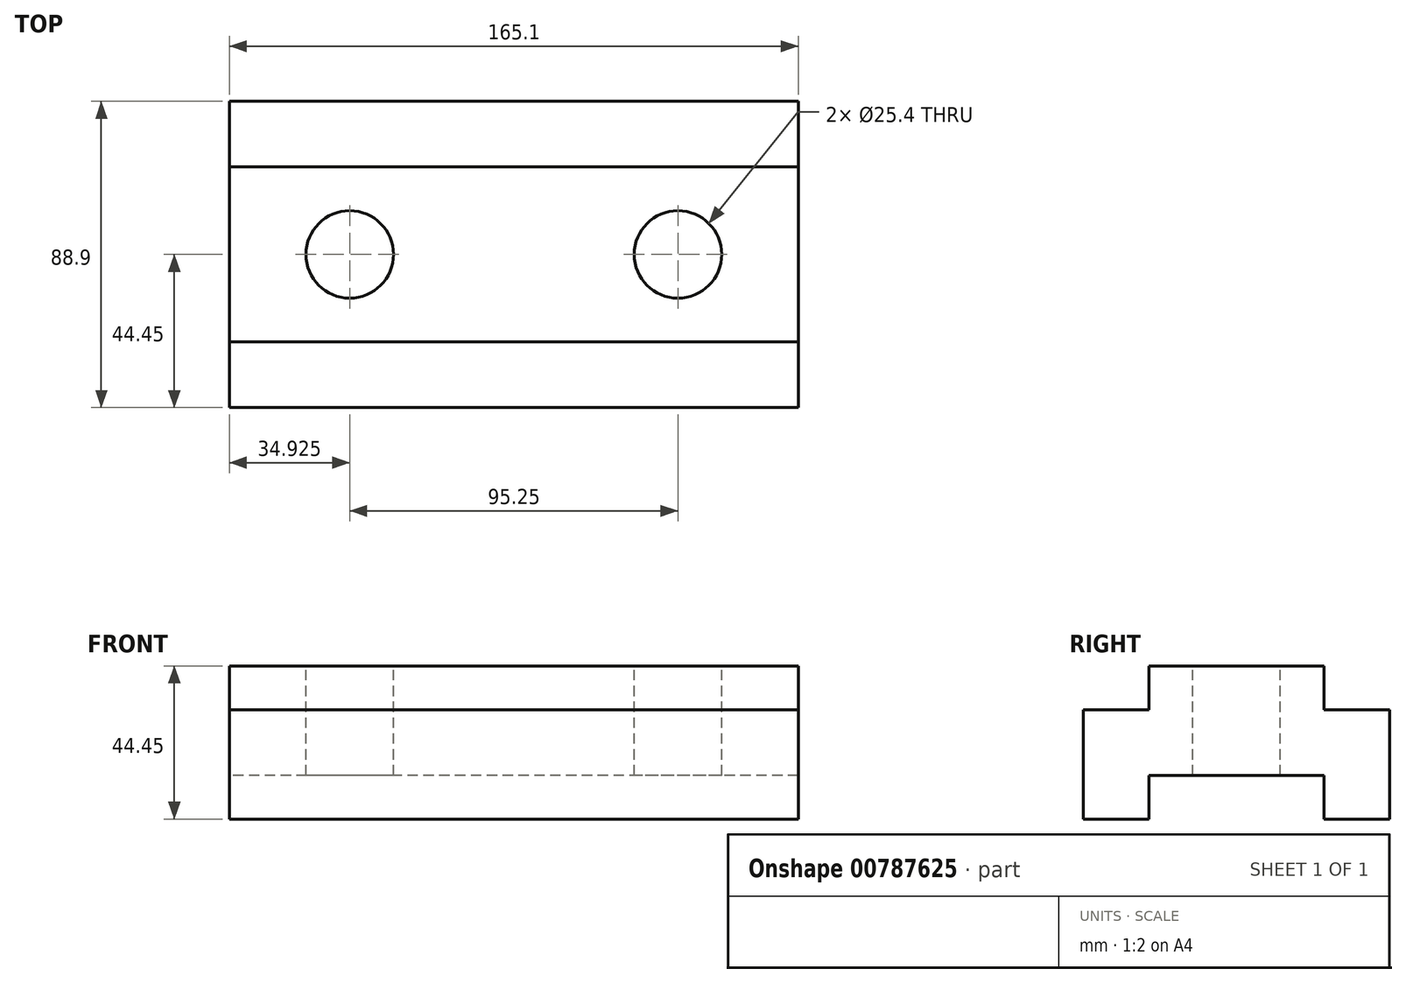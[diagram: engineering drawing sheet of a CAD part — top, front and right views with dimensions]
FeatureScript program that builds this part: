
annotation { "Feature Type Name" : "Feature", "Feature Type Description" : "" }
export const myFeature = defineFeature(function(context is Context, id is Id, definition is map)
    precondition{}
    {
        {
            var Q0;
            Q0=qCreatedBy(makeId("Right.planeOp"),FACE);
            var sketch = newSketch(context, id + "F0", { "sketchPlane" : qUnion([Q0])});
            skLineSegment(sketch, "E0", {"start": v(0, 0) * mm, "end": v(19.05, 0) * mm});
            skLineSegment(sketch, "E1", {"start": v(19.05, 0) * mm, "end": v(19.05, 12.7) * mm});
            skLineSegment(sketch, "E2", {"start": v(19.05, 12.7) * mm, "end": v(69.85, 12.7) * mm});
            skLineSegment(sketch, "E3", {"start": v(69.85, 12.7) * mm, "end": v(69.85, 0) * mm});
            skLineSegment(sketch, "E4", {"start": v(69.85, 0) * mm, "end": v(88.9, 0) * mm});
            skLineSegment(sketch, "E5", {"start": v(88.9, 0) * mm, "end": v(88.9, 31.75) * mm});
            skLineSegment(sketch, "E6", {"start": v(0, 0) * mm, "end": v(0, 31.75) * mm});
            skLineSegment(sketch, "E7", {"start": v(0, 31.75) * mm, "end": v(19.05, 31.75) * mm});
            skLineSegment(sketch, "E8", {"start": v(19.05, 31.75) * mm, "end": v(19.05, 44.45) * mm});
            skLineSegment(sketch, "E9", {"start": v(19.05, 44.45) * mm, "end": v(69.85, 44.45) * mm});
            skLineSegment(sketch, "E10", {"start": v(69.85, 44.45) * mm, "end": v(69.85, 31.75) * mm});
            skLineSegment(sketch, "E11", {"start": v(69.85, 31.75) * mm, "end": v(88.9, 31.75) * mm});
            skSolve(sketch);
        }
        {
            var Q0;
            Q0=makeQuery(id+"F0.imprint","IMPRINT",FACE,{"disambiguationData":[TD([[makeQuery(id+"F0.imprint","IMPRINT",EDGE,{"derivedFrom":sQuery(id+"F0.wireOp",EDGE,"E0")}),1.0]])]});
            extrude(context, id + "F1", {"entities" : qUnion([Q0]), "depth" : 165.1 * mm, "offsetDistance" : 25.4 * mm});
        }
        {
            var Q0;
            Q0=makeQuery(id+"F1.opExtrude","SWEPT_FACE",FACE,{"disambiguationData":[OSD([sQuery(id+"F0.wireOp",EDGE,"E9")])]});
            var sketch = newSketch(context, id + "F2", { "sketchPlane" : qUnion([Q0])});
            skLineSegment(sketch, "E12", {"start": v(0, 44.45) * mm, "end": v(34.92, 44.45) * mm, "construction": true});
            skLineSegment(sketch, "E13", {"start": v(34.92, 44.45) * mm, "end": v(130.18, 44.45) * mm, "construction": true});
            skCircle(sketch, "E14", {"center": v(34.92, 44.45) * mm, "radius": 12.7 * mm, "construction": true});
            skCircle(sketch, "E15", {"center": v(130.18, 44.45) * mm, "radius": 12.7 * mm, "construction": true});
            skCircle(sketch, "E16", {"center": v(34.92, 44.45) * mm, "radius": 12.7 * mm});
            skCircle(sketch, "E17", {"center": v(130.18, 44.45) * mm, "radius": 12.7 * mm});
            skSolve(sketch);
        }
        {
            var Q0;
            Q0=makeQuery(id+"F2.imprint","IMPRINT",FACE,{"disambiguationData":[TD([[makeQuery(id+"F2.imprint","IMPRINT",EDGE,{"derivedFrom":sQuery(id+"F2.wireOp",EDGE,"E16")}),1.0]])]});
            var Q1;
            Q1=makeQuery(id+"F2.imprint","IMPRINT",FACE,{"disambiguationData":[TD([[makeQuery(id+"F2.imprint","IMPRINT",EDGE,{"derivedFrom":sQuery(id+"F2.wireOp",EDGE,"E17")}),1.0]])]});
            extrude(context, id + "F3", {"entities" : qUnion([Q0, Q1]), "operationType" : NewBodyOperationType.REMOVE, "endBound" : BoundingType.THROUGH_ALL, "oppositeDirection" : true, "depth" : 25.4 * mm, "offsetDistance" : 25.4 * mm});
        }
    });
